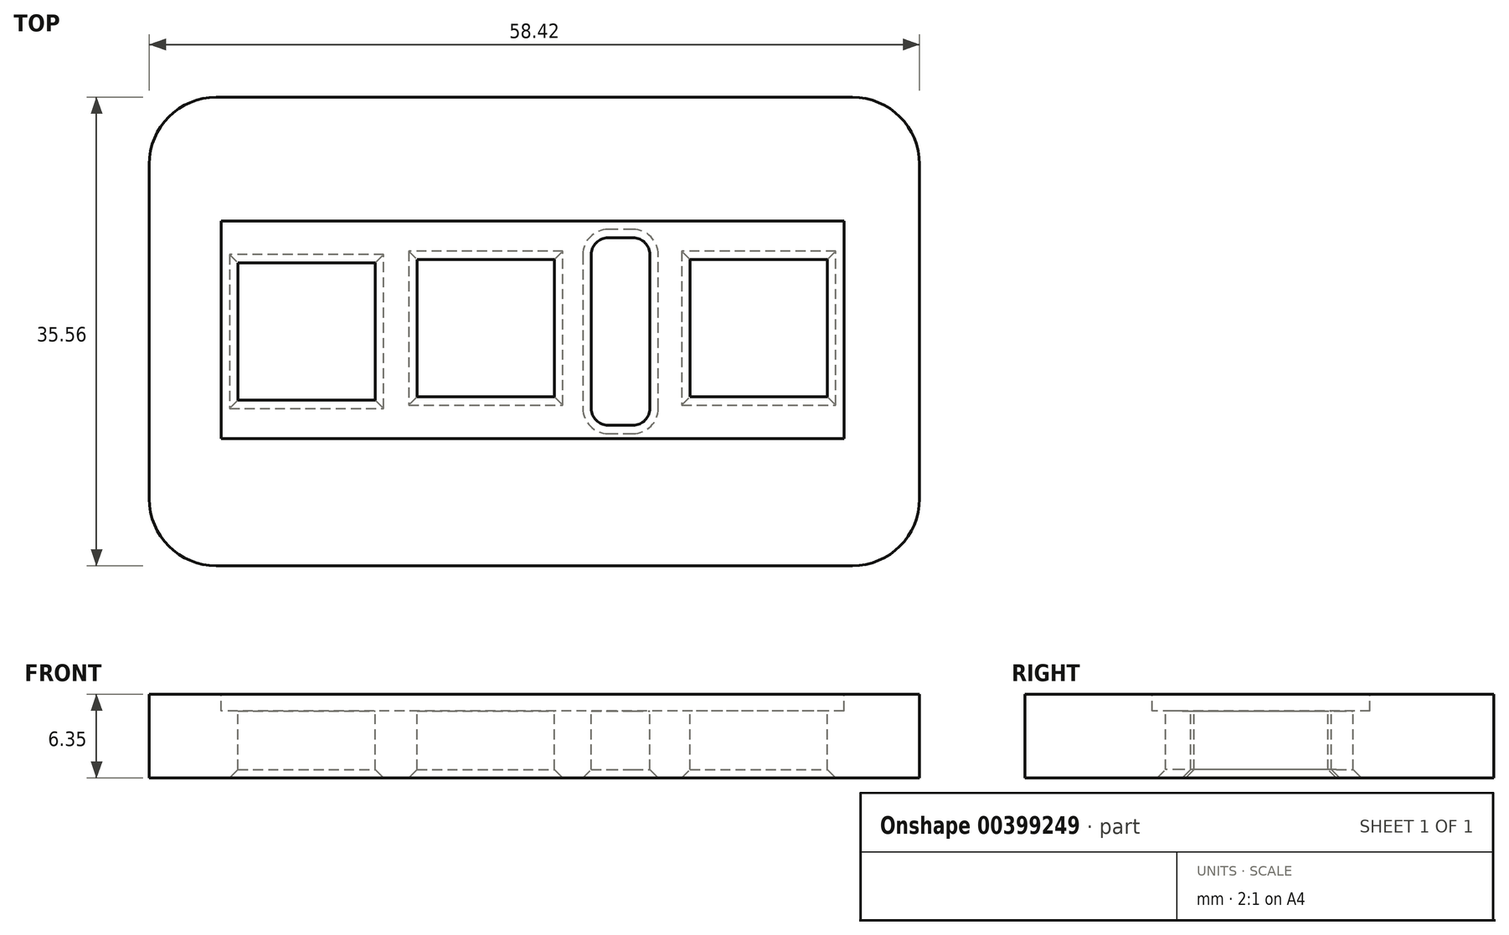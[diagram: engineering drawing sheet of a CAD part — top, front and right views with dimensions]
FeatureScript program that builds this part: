
annotation { "Feature Type Name" : "Feature", "Feature Type Description" : "" }
export const myFeature = defineFeature(function(context is Context, id is Id, definition is map)
    precondition{}
    {
        {
            var Q0;
            Q0=qCreatedBy(makeId("Top.planeOp"),FACE);
            var sketch = newSketch(context, id + "F0", { "sketchPlane" : qUnion([Q0])});
            skLineSegment(sketch, "E0.bottom", {"start": v(-40.81, -34) * mm, "end": v(-99.23, -34) * mm});
            skLineSegment(sketch, "E0.top", {"start": v(-40.81, 1.57) * mm, "end": v(-99.23, 1.57) * mm});
            skLineSegment(sketch, "E0.left", {"start": v(-40.81, -34) * mm, "end": v(-40.81, 1.57) * mm});
            skLineSegment(sketch, "E0.right", {"start": v(-99.23, -34) * mm, "end": v(-99.23, 1.57) * mm});
            skSolve(sketch);
        }
        {
            var Q0;
            Q0=makeQuery(id+"F0.imprint","IMPRINT",FACE,{"disambiguationData":[TD([[makeQuery(id+"F0.imprint","IMPRINT",EDGE,{"derivedFrom":sQuery(id+"F0.wireOp",EDGE,"E0.bottom")}),-1.0]])]});
            extrude(context, id + "F1", {"entities" : qUnion([Q0]), "depth" : 6.35 * mm});
        }
        {
            var Q0;
            Q0=makeQuery(id+"F1.opExtrude","CAP_FACE",FACE,{"disambiguationData":[OSD([sQuery(id+"F0.wireOp",EDGE,"E0.bottom"),sQuery(id+"F0.wireOp",EDGE,"E0.top"),sQuery(id+"F0.wireOp",EDGE,"E0.left"),sQuery(id+"F0.wireOp",EDGE,"E0.right")])],"isStart":false});
            var sketch = newSketch(context, id + "F2", { "sketchPlane" : qUnion([Q0])});
            skSolve(sketch);
        }
        {
            var Q0;
            Q0=makeQuery(id+"F2.imprint","IMPRINT",FACE,{"disambiguationData":[TD([[makeQuery(id+"F2.imprint","IMPRINT",EDGE,{"derivedFrom":makeQuery(id+"F1.opExtrude","CAP_EDGE",EDGE,{"disambiguationData":[OSD([sQuery(id+"F0.wireOp",EDGE,"E0.bottom")])],"isStart":false})}),-1.0]])]});
            var sketch = newSketch(context, id + "F3", { "sketchPlane" : qUnion([Q0])});
            skLineSegment(sketch, "E1.bottom", {"start": v(-46.53, -7.83) * mm, "end": v(-93.77, -7.83) * mm});
            skLineSegment(sketch, "E1.top", {"start": v(-46.53, -24.34) * mm, "end": v(-93.77, -24.34) * mm});
            skLineSegment(sketch, "E1.left", {"start": v(-46.53, -7.83) * mm, "end": v(-46.53, -24.34) * mm});
            skLineSegment(sketch, "E1.right", {"start": v(-93.77, -7.83) * mm, "end": v(-93.77, -24.34) * mm});
            skPoint(sketch, "E1.middle", {"position": v(-70.15, -16.08) * mm});
            skSolve(sketch);
        }
        {
            var Q0;
            Q0=makeQuery(id+"F2.imprint","IMPRINT",FACE,{"disambiguationData":[TD([[makeQuery(id+"F2.imprint","IMPRINT",EDGE,{"derivedFrom":makeQuery(id+"F1.opExtrude","CAP_EDGE",EDGE,{"disambiguationData":[OSD([sQuery(id+"F0.wireOp",EDGE,"E0.bottom")])],"isStart":false})}),-1.0]])]});
            var sketch = newSketch(context, id + "F4", { "sketchPlane" : qUnion([Q0])});
            skLineSegment(sketch, "E2.bottom", {"start": v(-82.09, -11) * mm, "end": v(-92.5, -11) * mm});
            skLineSegment(sketch, "E2.top", {"start": v(-82.09, -21.42) * mm, "end": v(-92.5, -21.42) * mm});
            skLineSegment(sketch, "E2.left", {"start": v(-82.09, -11) * mm, "end": v(-82.09, -21.42) * mm});
            skLineSegment(sketch, "E2.right", {"start": v(-92.5, -11) * mm, "end": v(-92.5, -21.42) * mm});
            skPoint(sketch, "E2.middle", {"position": v(-87.3, -16.21) * mm});
            skLineSegment(sketch, "E3.bottom", {"start": v(-68.5, -10.75) * mm, "end": v(-78.91, -10.75) * mm});
            skLineSegment(sketch, "E3.top", {"start": v(-68.5, -21.16) * mm, "end": v(-78.91, -21.16) * mm});
            skLineSegment(sketch, "E3.left", {"start": v(-68.5, -10.75) * mm, "end": v(-68.5, -21.16) * mm});
            skLineSegment(sketch, "E3.right", {"start": v(-78.91, -10.75) * mm, "end": v(-78.91, -21.16) * mm});
            skPoint(sketch, "E3.middle", {"position": v(-73.7, -15.96) * mm});
            skLineSegment(sketch, "E4.bottom", {"start": v(-58.21, -10.75) * mm, "end": v(-47.8, -10.75) * mm});
            skLineSegment(sketch, "E4.top", {"start": v(-58.21, -21.16) * mm, "end": v(-47.8, -21.16) * mm});
            skLineSegment(sketch, "E4.left", {"start": v(-58.21, -10.75) * mm, "end": v(-58.21, -21.16) * mm});
            skLineSegment(sketch, "E4.right", {"start": v(-47.8, -10.75) * mm, "end": v(-47.8, -21.16) * mm});
            skPoint(sketch, "E4.middle", {"position": v(-53, -15.96) * mm});
            skLineSegment(sketch, "E5.bottom", {"start": v(-61.26, -9.1) * mm, "end": v(-65.7, -9.1) * mm});
            skLineSegment(sketch, "E5.top", {"start": v(-61.26, -23.32) * mm, "end": v(-65.7, -23.32) * mm});
            skLineSegment(sketch, "E5.left", {"start": v(-61.26, -9.1) * mm, "end": v(-61.26, -23.32) * mm});
            skLineSegment(sketch, "E5.right", {"start": v(-65.7, -9.1) * mm, "end": v(-65.7, -23.32) * mm});
            skPoint(sketch, "E5.middle", {"position": v(-63.48, -16.21) * mm});
            skSolve(sketch);
        }
        {
            var Q0;
            Q0 = qSketchRegion(id + "F4", true);
            extrude(context, id + "F5", {"entities" : qUnion([Q0]), "operationType" : NewBodyOperationType.REMOVE, "oppositeDirection" : true, "depth" : 25.4 * mm});
        }
        {
            var Q0;
            Q0=makeQuery(id+"F5.boolean.opBoolean","COPY",EDGE,{"derivedFrom":makeQuery(id+"F5.opExtrude","SWEPT_EDGE",EDGE,{"disambiguationData":[OSD([sQuery(id+"F4.wireOp",EDGE,"E5.bottom"),sQuery(id+"F4.wireOp",EDGE,"E5.right")])]})});
            var Q1;
            Q1=makeQuery(id+"F5.boolean.opBoolean","COPY",EDGE,{"derivedFrom":makeQuery(id+"F5.opExtrude","SWEPT_EDGE",EDGE,{"disambiguationData":[OSD([sQuery(id+"F4.wireOp",EDGE,"E5.bottom"),sQuery(id+"F4.wireOp",EDGE,"E5.left")])]})});
            var Q2;
            Q2=makeQuery(id+"F5.boolean.opBoolean","COPY",EDGE,{"derivedFrom":makeQuery(id+"F5.opExtrude","SWEPT_EDGE",EDGE,{"disambiguationData":[OSD([sQuery(id+"F4.wireOp",EDGE,"E5.top"),sQuery(id+"F4.wireOp",EDGE,"E5.left")])]})});
            var Q3;
            Q3=makeQuery(id+"F5.boolean.opBoolean","COPY",EDGE,{"derivedFrom":makeQuery(id+"F5.opExtrude","SWEPT_EDGE",EDGE,{"disambiguationData":[OSD([sQuery(id+"F4.wireOp",EDGE,"E5.top"),sQuery(id+"F4.wireOp",EDGE,"E5.right")])]})});
            fillet(context, id + "F6", {"entities" : qUnion([Q0, Q1, Q2, Q3]), "radius" : 1.27 * mm, "tangentPropagation" : true, "allowEdgeOverflow" : false});
        }
        {
            var Q0;
            Q0 = qSketchRegion(id + "F3", true);
            extrude(context, id + "F7", {"entities" : qUnion([Q0]), "operationType" : NewBodyOperationType.REMOVE, "oppositeDirection" : true, "depth" : 1.27 * mm});
        }
        {
            var Q0;
            Q0=makeQuery(id+"F1.opExtrude","SWEPT_EDGE",EDGE,{"disambiguationData":[OSD([sQuery(id+"F0.wireOp",EDGE,"E0.bottom"),sQuery(id+"F0.wireOp",EDGE,"E0.left")])]});
            var Q1;
            Q1=makeQuery(id+"F1.opExtrude","SWEPT_EDGE",EDGE,{"disambiguationData":[OSD([sQuery(id+"F0.wireOp",EDGE,"E0.top"),sQuery(id+"F0.wireOp",EDGE,"E0.left")])]});
            var Q2;
            Q2=makeQuery(id+"F1.opExtrude","SWEPT_EDGE",EDGE,{"disambiguationData":[OSD([sQuery(id+"F0.wireOp",EDGE,"E0.bottom"),sQuery(id+"F0.wireOp",EDGE,"E0.right")])]});
            var Q3;
            Q3=makeQuery(id+"F1.opExtrude","SWEPT_EDGE",EDGE,{"disambiguationData":[OSD([sQuery(id+"F0.wireOp",EDGE,"E0.top"),sQuery(id+"F0.wireOp",EDGE,"E0.right")])]});
            fillet(context, id + "F8", {"entities" : qUnion([Q0, Q1, Q2, Q3]), "radius" : 5.08 * mm, "tangentPropagation" : true, "allowEdgeOverflow" : false});
        }
        {
            var Q0;
            Q0=makeQuery(id+"F5.boolean.opBoolean","INTERSECT",EDGE,{"derivedFrom":[makeQuery(id+"F1.opExtrude","CAP_FACE",FACE,{"disambiguationData":[OSD([sQuery(id+"F0.wireOp",EDGE,"E0.bottom"),sQuery(id+"F0.wireOp",EDGE,"E0.top"),sQuery(id+"F0.wireOp",EDGE,"E0.left"),sQuery(id+"F0.wireOp",EDGE,"E0.right")])],"isStart":true}),makeQuery(id+"F5.opExtrude","SWEPT_FACE",FACE,{"disambiguationData":[OSD([sQuery(id+"F4.wireOp",EDGE,"E2.top")])]})]});
            var Q1;
            Q1=makeQuery(id+"F5.boolean.opBoolean","INTERSECT",EDGE,{"derivedFrom":[makeQuery(id+"F1.opExtrude","CAP_FACE",FACE,{"disambiguationData":[OSD([sQuery(id+"F0.wireOp",EDGE,"E0.bottom"),sQuery(id+"F0.wireOp",EDGE,"E0.top"),sQuery(id+"F0.wireOp",EDGE,"E0.left"),sQuery(id+"F0.wireOp",EDGE,"E0.right")])],"isStart":true}),makeQuery(id+"F5.opExtrude","SWEPT_FACE",FACE,{"disambiguationData":[OSD([sQuery(id+"F4.wireOp",EDGE,"E2.bottom")])]})]});
            var Q2;
            Q2=makeQuery(id+"F5.boolean.opBoolean","INTERSECT",EDGE,{"derivedFrom":[makeQuery(id+"F1.opExtrude","CAP_FACE",FACE,{"disambiguationData":[OSD([sQuery(id+"F0.wireOp",EDGE,"E0.bottom"),sQuery(id+"F0.wireOp",EDGE,"E0.top"),sQuery(id+"F0.wireOp",EDGE,"E0.left"),sQuery(id+"F0.wireOp",EDGE,"E0.right")])],"isStart":true}),makeQuery(id+"F5.opExtrude","SWEPT_FACE",FACE,{"disambiguationData":[OSD([sQuery(id+"F4.wireOp",EDGE,"E2.left")])]})]});
            var Q3;
            Q3=makeQuery(id+"F5.boolean.opBoolean","INTERSECT",EDGE,{"derivedFrom":[makeQuery(id+"F1.opExtrude","CAP_FACE",FACE,{"disambiguationData":[OSD([sQuery(id+"F0.wireOp",EDGE,"E0.bottom"),sQuery(id+"F0.wireOp",EDGE,"E0.top"),sQuery(id+"F0.wireOp",EDGE,"E0.left"),sQuery(id+"F0.wireOp",EDGE,"E0.right")])],"isStart":true}),makeQuery(id+"F5.opExtrude","SWEPT_FACE",FACE,{"disambiguationData":[OSD([sQuery(id+"F4.wireOp",EDGE,"E2.right")])]})]});
            var Q4;
            Q4=makeQuery(id+"F5.boolean.opBoolean","INTERSECT",EDGE,{"derivedFrom":[makeQuery(id+"F1.opExtrude","CAP_FACE",FACE,{"disambiguationData":[OSD([sQuery(id+"F0.wireOp",EDGE,"E0.bottom"),sQuery(id+"F0.wireOp",EDGE,"E0.top"),sQuery(id+"F0.wireOp",EDGE,"E0.left"),sQuery(id+"F0.wireOp",EDGE,"E0.right")])],"isStart":true}),makeQuery(id+"F5.opExtrude","SWEPT_FACE",FACE,{"disambiguationData":[OSD([sQuery(id+"F4.wireOp",EDGE,"E3.top")])]})]});
            var Q5;
            Q5=makeQuery(id+"F5.boolean.opBoolean","INTERSECT",EDGE,{"derivedFrom":[makeQuery(id+"F1.opExtrude","CAP_FACE",FACE,{"disambiguationData":[OSD([sQuery(id+"F0.wireOp",EDGE,"E0.bottom"),sQuery(id+"F0.wireOp",EDGE,"E0.top"),sQuery(id+"F0.wireOp",EDGE,"E0.left"),sQuery(id+"F0.wireOp",EDGE,"E0.right")])],"isStart":true}),makeQuery(id+"F5.opExtrude","SWEPT_FACE",FACE,{"disambiguationData":[OSD([sQuery(id+"F4.wireOp",EDGE,"E3.right")])]})]});
            var Q6;
            Q6=makeQuery(id+"F5.boolean.opBoolean","INTERSECT",EDGE,{"derivedFrom":[makeQuery(id+"F1.opExtrude","CAP_FACE",FACE,{"disambiguationData":[OSD([sQuery(id+"F0.wireOp",EDGE,"E0.bottom"),sQuery(id+"F0.wireOp",EDGE,"E0.top"),sQuery(id+"F0.wireOp",EDGE,"E0.left"),sQuery(id+"F0.wireOp",EDGE,"E0.right")])],"isStart":true}),makeQuery(id+"F5.opExtrude","SWEPT_FACE",FACE,{"disambiguationData":[OSD([sQuery(id+"F4.wireOp",EDGE,"E3.bottom")])]})]});
            var Q7;
            Q7=makeQuery(id+"F5.boolean.opBoolean","INTERSECT",EDGE,{"derivedFrom":[makeQuery(id+"F1.opExtrude","CAP_FACE",FACE,{"disambiguationData":[OSD([sQuery(id+"F0.wireOp",EDGE,"E0.bottom"),sQuery(id+"F0.wireOp",EDGE,"E0.top"),sQuery(id+"F0.wireOp",EDGE,"E0.left"),sQuery(id+"F0.wireOp",EDGE,"E0.right")])],"isStart":true}),makeQuery(id+"F5.opExtrude","SWEPT_FACE",FACE,{"disambiguationData":[OSD([sQuery(id+"F4.wireOp",EDGE,"E3.left")])]})]});
            var Q8;
            Q8=makeQuery(id+"F5.boolean.opBoolean","INTERSECT",EDGE,{"derivedFrom":[makeQuery(id+"F1.opExtrude","CAP_FACE",FACE,{"disambiguationData":[OSD([sQuery(id+"F0.wireOp",EDGE,"E0.bottom"),sQuery(id+"F0.wireOp",EDGE,"E0.top"),sQuery(id+"F0.wireOp",EDGE,"E0.left"),sQuery(id+"F0.wireOp",EDGE,"E0.right")])],"isStart":true}),makeQuery(id+"F5.opExtrude","SWEPT_FACE",FACE,{"disambiguationData":[OSD([sQuery(id+"F4.wireOp",EDGE,"E5.right")])]})]});
            var Q9;
            Q9=makeQuery(id+"F5.boolean.opBoolean","INTERSECT",EDGE,{"derivedFrom":[makeQuery(id+"F1.opExtrude","CAP_FACE",FACE,{"disambiguationData":[OSD([sQuery(id+"F0.wireOp",EDGE,"E0.bottom"),sQuery(id+"F0.wireOp",EDGE,"E0.top"),sQuery(id+"F0.wireOp",EDGE,"E0.left"),sQuery(id+"F0.wireOp",EDGE,"E0.right")])],"isStart":true}),makeQuery(id+"F5.opExtrude","SWEPT_FACE",FACE,{"disambiguationData":[OSD([sQuery(id+"F4.wireOp",EDGE,"E4.left")])]})]});
            var Q10;
            Q10=makeQuery(id+"F5.boolean.opBoolean","INTERSECT",EDGE,{"derivedFrom":[makeQuery(id+"F1.opExtrude","CAP_FACE",FACE,{"disambiguationData":[OSD([sQuery(id+"F0.wireOp",EDGE,"E0.bottom"),sQuery(id+"F0.wireOp",EDGE,"E0.top"),sQuery(id+"F0.wireOp",EDGE,"E0.left"),sQuery(id+"F0.wireOp",EDGE,"E0.right")])],"isStart":true}),makeQuery(id+"F5.opExtrude","SWEPT_FACE",FACE,{"disambiguationData":[OSD([sQuery(id+"F4.wireOp",EDGE,"E4.top")])]})]});
            var Q11;
            Q11=makeQuery(id+"F5.boolean.opBoolean","INTERSECT",EDGE,{"derivedFrom":[makeQuery(id+"F1.opExtrude","CAP_FACE",FACE,{"disambiguationData":[OSD([sQuery(id+"F0.wireOp",EDGE,"E0.bottom"),sQuery(id+"F0.wireOp",EDGE,"E0.top"),sQuery(id+"F0.wireOp",EDGE,"E0.left"),sQuery(id+"F0.wireOp",EDGE,"E0.right")])],"isStart":true}),makeQuery(id+"F5.opExtrude","SWEPT_FACE",FACE,{"disambiguationData":[OSD([sQuery(id+"F4.wireOp",EDGE,"E4.right")])]})]});
            var Q12;
            Q12=makeQuery(id+"F5.boolean.opBoolean","INTERSECT",EDGE,{"derivedFrom":[makeQuery(id+"F1.opExtrude","CAP_FACE",FACE,{"disambiguationData":[OSD([sQuery(id+"F0.wireOp",EDGE,"E0.bottom"),sQuery(id+"F0.wireOp",EDGE,"E0.top"),sQuery(id+"F0.wireOp",EDGE,"E0.left"),sQuery(id+"F0.wireOp",EDGE,"E0.right")])],"isStart":true}),makeQuery(id+"F5.opExtrude","SWEPT_FACE",FACE,{"disambiguationData":[OSD([sQuery(id+"F4.wireOp",EDGE,"E4.bottom")])]})]});
            chamfer(context, id + "F9", {"entities" : qUnion([Q0, Q1, Q2, Q3, Q4, Q5, Q6, Q7, Q8, Q9, Q10, Q11, Q12]), "width" : 0.64 * mm, "tangentPropagation" : true});
        }
    });
